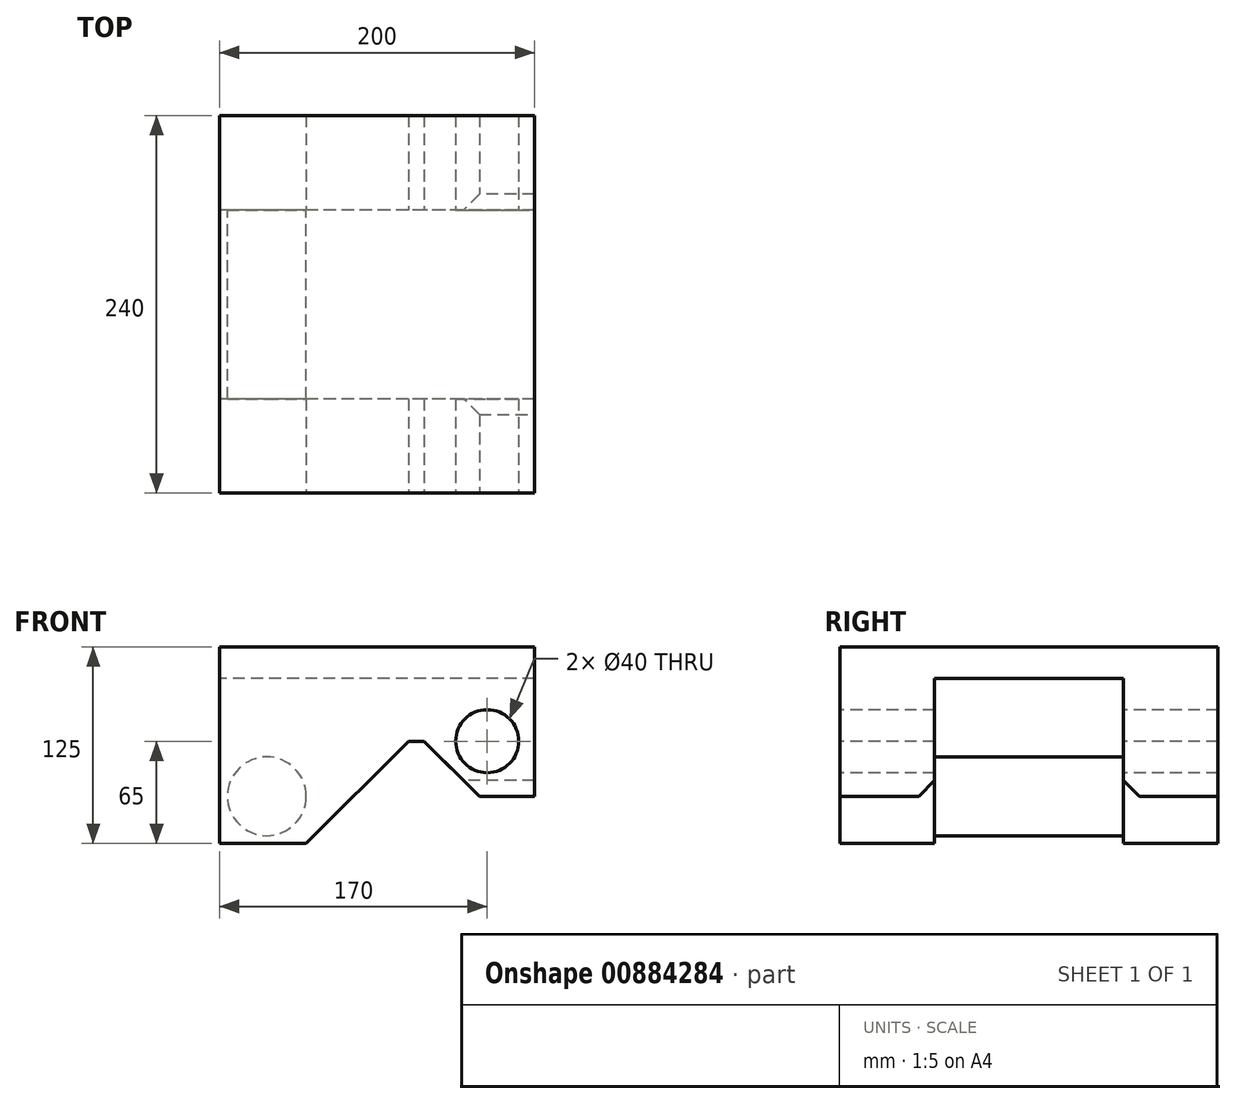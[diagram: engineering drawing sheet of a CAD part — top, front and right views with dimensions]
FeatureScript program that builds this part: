
annotation { "Feature Type Name" : "Feature", "Feature Type Description" : "" }
export const myFeature = defineFeature(function(context is Context, id is Id, definition is map)
    precondition{}
    {
        {
            var Q0;
            Q0=qCreatedBy(makeId("Right.planeOp"),FACE);
            var sketch = newSketch(context, id + "F0", { "sketchPlane" : qUnion([Q0])});
            skLineSegment(sketch, "E0", {"start": v(-120, -30) * mm, "end": v(-120, 95) * mm});
            skLineSegment(sketch, "E1", {"start": v(-120, 95) * mm, "end": v(0, 95) * mm});
            skLineSegment(sketch, "E2", {"start": v(0, 0) * mm, "end": v(0, 113.74) * mm, "construction": true});
            skLineSegment(sketch, "E3", {"start": v(-120, -30) * mm, "end": v(-60, -30) * mm});
            skLineSegment(sketch, "E4", {"start": v(-60, -30) * mm, "end": v(-60, 75) * mm});
            skLineSegment(sketch, "E5", {"start": v(-60, 75) * mm, "end": v(0, 75) * mm});
            skLineSegment(sketch, "E6.MirrorCS", {"start": v(60, 75) * mm, "end": v(0, 75) * mm});
            skLineSegment(sketch, "E7.MirrorCS", {"start": v(60, -30) * mm, "end": v(60, 75) * mm});
            skLineSegment(sketch, "E8.MirrorCS", {"start": v(120, 95) * mm, "end": v(0, 95) * mm});
            skLineSegment(sketch, "E9.MirrorCS", {"start": v(120, -30) * mm, "end": v(60, -30) * mm});
            skLineSegment(sketch, "E10.MirrorCS", {"start": v(120, -30) * mm, "end": v(120, 95) * mm});
            skSolve(sketch);
        }
        {
            var Q0;
            Q0=makeQuery(id+"F0.imprint","IMPRINT",FACE,{"disambiguationData":[TD([[makeQuery(id+"F0.imprint","IMPRINT",EDGE,{"derivedFrom":sQuery(id+"F0.wireOp",EDGE,"E0")}),-1.0]])]});
            extrude(context, id + "F1", {"entities" : qUnion([Q0]), "depth" : 170 * mm, "offsetDistance" : 25 * mm, "hasSecondDirection" : true, "secondDirectionOppositeDirection" : true, "secondDirectionDepth" : 30 * mm});
        }
        {
            var Q0;
            Q0=qCreatedBy(makeId("Front.planeOp"),FACE);
            var sketch = newSketch(context, id + "F2", { "sketchPlane" : qUnion([Q0])});
            skCircle(sketch, "E11", {"center": v(0, 0) * mm, "radius": 25 * mm});
            skLineSegment(sketch, "E12", {"start": v(0, 0) * mm, "end": v(0, 106.29) * mm, "construction": true});
            skSolve(sketch);
        }
        {
            var Q0;
            Q0=makeQuery(id+"F2.imprint","IMPRINT",FACE,{"disambiguationData":[TD([[makeQuery(id+"F2.imprint","IMPRINT",EDGE,{"derivedFrom":sQuery(id+"F2.wireOp",EDGE,"e0081abd-0d2f-43d0-91b7-deafed7ec2df0.MirrorC")}),-1.0]])]});
            var Q1;
            Q1=makeQuery(id+"F2.imprint","IMPRINT",FACE,{"disambiguationData":[TD([[makeQuery(id+"F2.imprint","IMPRINT",EDGE,{"derivedFrom":sQuery(id+"F2.wireOp",EDGE,"E11")}),1.0]])]});
            extrude(context, id + "F3", {"entities" : qUnion([Q0, Q1]), "operationType" : NewBodyOperationType.ADD, "endBound" : BoundingType.UP_TO_NEXT, "depth" : 25 * mm, "offsetDistance" : 25 * mm, "hasSecondDirection" : true, "secondDirectionBound" : SecondDirectionBoundingType.UP_TO_NEXT, "secondDirectionOppositeDirection" : true, "secondDirectionDepth" : 25 * mm});
        }
        {
            var Q0;
            Q0=qCreatedBy(makeId("Front.planeOp"),FACE);
            var sketch = newSketch(context, id + "F4", { "sketchPlane" : qUnion([Q0])});
            skLineSegment(sketch, "E13", {"start": v(170, 0) * mm, "end": v(135, 0) * mm});
            skLineSegment(sketch, "E14", {"start": v(135, 0) * mm, "end": v(100, 35) * mm});
            skLineSegment(sketch, "E15", {"start": v(100, 35) * mm, "end": v(90, 35) * mm});
            skLineSegment(sketch, "E16", {"start": v(90, 35) * mm, "end": v(25, -30) * mm});
            skLineSegment(sketch, "E17", {"start": v(170, 0) * mm, "end": v(170, -30) * mm});
            skLineSegment(sketch, "E18", {"start": v(170, -30) * mm, "end": v(25, -30) * mm});
            skSolve(sketch);
        }
        {
            var Q0;
            Q0=makeQuery(id+"F4.imprint","IMPRINT",FACE,{"disambiguationData":[TD([[makeQuery(id+"F4.imprint","IMPRINT",EDGE,{"derivedFrom":sQuery(id+"F4.wireOp",EDGE,"E13")}),1.0]])]});
            extrude(context, id + "F5", {"entities" : qUnion([Q0]), "operationType" : NewBodyOperationType.REMOVE, "endBound" : BoundingType.THROUGH_ALL, "oppositeDirection" : true, "depth" : 25 * mm, "offsetDistance" : 25 * mm, "hasSecondDirection" : true, "secondDirectionBound" : SecondDirectionBoundingType.THROUGH_ALL, "secondDirectionOppositeDirection" : false, "secondDirectionDepth" : 25 * mm});
        }
        {
            var Q0;
            Q0=qCreatedBy(makeId("Front.planeOp"),FACE);
            var sketch = newSketch(context, id + "F6", { "sketchPlane" : qUnion([Q0])});
            skCircle(sketch, "E19", {"center": v(140, 35) * mm, "radius": 20 * mm});
            skSolve(sketch);
        }
        {
            var Q0;
            Q0=makeQuery(id+"F6.imprint","IMPRINT",FACE,{"disambiguationData":[TD([[makeQuery(id+"F6.imprint","IMPRINT",EDGE,{"derivedFrom":sQuery(id+"F6.wireOp",EDGE,"E19")}),1.0]])]});
            extrude(context, id + "F7", {"entities" : qUnion([Q0]), "operationType" : NewBodyOperationType.REMOVE, "endBound" : BoundingType.THROUGH_ALL, "oppositeDirection" : true, "depth" : 25 * mm, "offsetDistance" : 25 * mm, "hasSecondDirection" : true, "secondDirectionBound" : SecondDirectionBoundingType.THROUGH_ALL, "secondDirectionOppositeDirection" : false, "secondDirectionDepth" : 25 * mm});
        }
        {
            var Q0;
            Q0=makeQuery(id+"F5.boolean.opBoolean","INTERSECT",EDGE,{"derivedFrom":[makeQuery(id+"F1.opExtrude","SWEPT_FACE",FACE,{"disambiguationData":[OSD([sQuery(id+"F0.wireOp",EDGE,"E4")])]}),makeQuery(id+"F5.opExtrude","SWEPT_FACE",FACE,{"disambiguationData":[OSD([sQuery(id+"F4.wireOp",EDGE,"E13")])]})]});
            var Q1;
            Q1=makeQuery(id+"F5.boolean.opBoolean","INTERSECT",EDGE,{"derivedFrom":[makeQuery(id+"F1.opExtrude","SWEPT_FACE",FACE,{"disambiguationData":[OSD([sQuery(id+"F0.wireOp",EDGE,"E7.MirrorCS")])]}),makeQuery(id+"F5.opExtrude","SWEPT_FACE",FACE,{"disambiguationData":[OSD([sQuery(id+"F4.wireOp",EDGE,"E13")])]})]});
            chamfer(context, id + "F8", {"entities" : qUnion([Q0, Q1]), "width" : 10 * mm, "tangentPropagation" : true});
        }
    });
